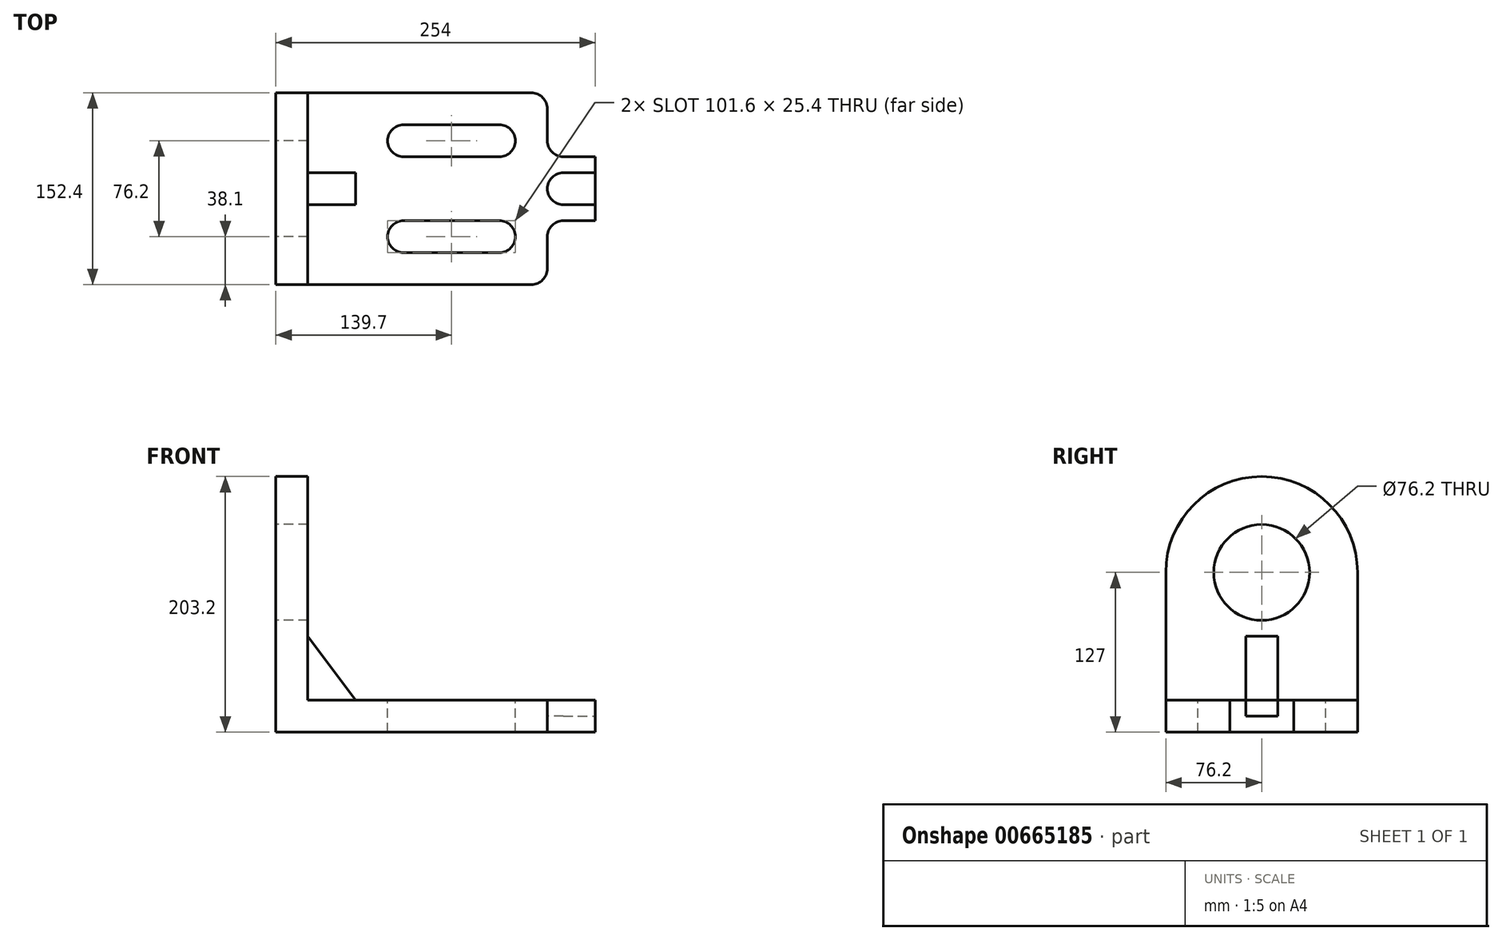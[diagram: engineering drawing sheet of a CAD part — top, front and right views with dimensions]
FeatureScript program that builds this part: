
annotation { "Feature Type Name" : "Feature", "Feature Type Description" : "" }
export const myFeature = defineFeature(function(context is Context, id is Id, definition is map)
    precondition{}
    {
        {
            var Q0;
            Q0=qCreatedBy(makeId("Top.planeOp"),FACE);
            var sketch = newSketch(context, id + "F0", { "sketchPlane" : qUnion([Q0])});
            skLineSegment(sketch, "E0", {"start": v(0, 0) * mm, "end": v(203.2, 0) * mm});
            skLineSegment(sketch, "E1", {"start": v(215.9, 12.7) * mm, "end": v(215.9, 38.1) * mm});
            skLineSegment(sketch, "E2", {"start": v(228.6, 50.8) * mm, "end": v(254, 50.8) * mm});
            skLineSegment(sketch, "E3", {"start": v(254, 50.8) * mm, "end": v(254, 101.6) * mm});
            skLineSegment(sketch, "E4", {"start": v(254, 101.6) * mm, "end": v(228.6, 101.6) * mm});
            skLineSegment(sketch, "E5", {"start": v(215.9, 114.3) * mm, "end": v(215.9, 139.7) * mm});
            skLineSegment(sketch, "E6", {"start": v(203.2, 152.4) * mm, "end": v(0, 152.4) * mm});
            skLineSegment(sketch, "E7", {"start": v(0, 152.4) * mm, "end": v(0, 0) * mm});
            skLineSegment(sketch, "E8", {"start": v(254, 76.2) * mm, "end": v(228.6, 76.2) * mm, "construction": true});
            skArc(sketch, "E9", {"start": v(228.6, 88.9) * mm, "mid": v(215.9, 76.2) * mm, "end": v(228.6, 63.5) * mm});
            skLineSegment(sketch, "E10", {"start": v(228.6, 88.9) * mm, "end": v(254, 88.9) * mm});
            skLineSegment(sketch, "E11", {"start": v(228.6, 63.5) * mm, "end": v(254, 63.5) * mm});
            skPoint(sketch, "E12.visualSharp", {"position": v(215.9, 152.4) * mm});
            skArc(sketch, "E12.filletArc", {"start": v(215.9, 139.7) * mm, "mid": v(212.18, 148.68) * mm, "end": v(203.2, 152.4) * mm});
            skPoint(sketch, "E13.visualSharp", {"position": v(215.9, 101.6) * mm});
            skArc(sketch, "E13.filletArc", {"start": v(215.9, 114.3) * mm, "mid": v(219.62, 105.32) * mm, "end": v(228.6, 101.6) * mm});
            skPoint(sketch, "E14.visualSharp", {"position": v(215.9, 50.8) * mm});
            skArc(sketch, "E14.filletArc", {"start": v(228.6, 50.8) * mm, "mid": v(219.62, 47.08) * mm, "end": v(215.9, 38.1) * mm});
            skPoint(sketch, "E15.visualSharp", {"position": v(215.9, 0) * mm});
            skArc(sketch, "E15.filletArc", {"start": v(203.2, 0) * mm, "mid": v(212.18, 3.72) * mm, "end": v(215.9, 12.7) * mm});
            skLineSegment(sketch, "E16.0", {"start": v(25.4, 38.1) * mm, "end": v(177.8, 38.1) * mm, "construction": true});
            skLineSegment(sketch, "E17.0", {"start": v(101.6, 114.3) * mm, "end": v(101.6, 38.1) * mm, "construction": true});
            skLineSegment(sketch, "E18.0", {"start": v(177.8, 114.3) * mm, "end": v(177.8, 38.1) * mm, "construction": true});
            skArc(sketch, "E19", {"start": v(177.8, 101.6) * mm, "mid": v(190.5, 114.3) * mm, "end": v(177.8, 127) * mm});
            skArc(sketch, "E20", {"start": v(101.6, 127) * mm, "mid": v(88.9, 114.3) * mm, "end": v(101.6, 101.6) * mm});
            skArc(sketch, "E21", {"start": v(177.8, 25.4) * mm, "mid": v(190.5, 38.1) * mm, "end": v(177.8, 50.8) * mm});
            skArc(sketch, "E22", {"start": v(101.6, 50.8) * mm, "mid": v(88.9, 38.1) * mm, "end": v(101.6, 25.4) * mm});
            skLineSegment(sketch, "E23", {"start": v(101.6, 127) * mm, "end": v(177.8, 127) * mm});
            skLineSegment(sketch, "E24", {"start": v(101.6, 101.6) * mm, "end": v(177.8, 101.6) * mm});
            skLineSegment(sketch, "E25", {"start": v(101.6, 50.8) * mm, "end": v(177.8, 50.8) * mm});
            skLineSegment(sketch, "E26", {"start": v(101.6, 25.4) * mm, "end": v(177.8, 25.4) * mm});
            skLineSegment(sketch, "E27.0", {"start": v(177.8, 114.3) * mm, "end": v(0, 114.3) * mm, "construction": true});
            skLineSegment(sketch, "E28.0", {"start": v(25.4, 152.4) * mm, "end": v(25.4, 0) * mm, "construction": true});
            skLineSegment(sketch, "E29.0", {"start": v(63.5, 88.9) * mm, "end": v(25.4, 88.9) * mm});
            skLineSegment(sketch, "E30.0", {"start": v(63.5, 63.5) * mm, "end": v(25.4, 63.5) * mm});
            skLineSegment(sketch, "E31", {"start": v(63.5, 88.9) * mm, "end": v(63.5, 63.5) * mm});
            skLineSegment(sketch, "E32", {"start": v(25.4, 88.9) * mm, "end": v(25.4, 63.5) * mm});
            skSolve(sketch);
        }
        {
            var Q0;
            Q0=makeQuery(id+"F0.imprint","IMPRINT",FACE,{"disambiguationData":[TD([[makeQuery(id+"F0.imprint","IMPRINT",EDGE,{"derivedFrom":sQuery(id+"F0.wireOp",EDGE,"E0")}),1.0]])]});
            var Q1;
            Q1=makeQuery(id+"F0.imprint","IMPRINT",FACE,{"disambiguationData":[TD([[makeQuery(id+"F0.imprint","IMPRINT",EDGE,{"derivedFrom":sQuery(id+"F0.wireOp",EDGE,"E9")}),1.0]])]});
            var Q2;
            Q2=makeQuery(id+"F0.imprint","IMPRINT",FACE,{"disambiguationData":[TD([[makeQuery(id+"F0.imprint","IMPRINT",EDGE,{"derivedFrom":sQuery(id+"F0.wireOp",EDGE,"E29.0")}),1.0]])]});
            extrude(context, id + "F1", {"entities" : qUnion([Q0, Q1, Q2]), "oppositeDirection" : true, "depth" : 25.4 * mm, "offsetDistance" : 25.4 * mm});
        }
        {
            var Q0;
            Q0=makeQuery(id+"F1.opExtrude","SWEPT_FACE",FACE,{"disambiguationData":[OSD([sQuery(id+"F0.wireOp",EDGE,"E7")])]});
            var sketch = newSketch(context, id + "F2", { "sketchPlane" : qUnion([Q0])});
            skPoint(sketch, "E33.centerSnap0", {"position": v(-76.2, 0) * mm});
            skLineSegment(sketch, "E34", {"start": v(-152.4, 0) * mm, "end": v(-152.4, 101.6) * mm});
            skLineSegment(sketch, "E35", {"start": v(0, 0) * mm, "end": v(0, 101.6) * mm});
            skArc(sketch, "E36", {"start": v(0, 101.6) * mm, "mid": v(-76.2, 177.8) * mm, "end": v(-152.4, 101.6) * mm});
            skCircle(sketch, "E37", {"center": v(-76.2, 101.6) * mm, "radius": 38.1 * mm});
            skSolve(sketch);
        }
        {
            var Q0;
            Q0=makeQuery(id+"F2.imprint","IMPRINT",FACE,{"disambiguationData":[TD([[makeQuery(id+"F2.imprint","IMPRINT",EDGE,{"derivedFrom":sQuery(id+"F2.wireOp",EDGE,"E34")}),-1.0]])]});
            extrude(context, id + "F3", {"entities" : qUnion([Q0]), "operationType" : NewBodyOperationType.ADD, "oppositeDirection" : true, "depth" : 25.4 * mm, "offsetDistance" : 25.4 * mm});
        }
        {
            var Q0;
            Q0=makeQuery(id+"F0.imprint","IMPRINT",FACE,{"disambiguationData":[TD([[makeQuery(id+"F0.imprint","IMPRINT",EDGE,{"derivedFrom":sQuery(id+"F0.wireOp",EDGE,"E9")}),1.0]])]});
            extrude(context, id + "F4", {"entities" : qUnion([Q0]), "operationType" : NewBodyOperationType.REMOVE, "oppositeDirection" : true, "depth" : 12.7 * mm, "offsetDistance" : 25.4 * mm});
        }
        {
            var Q0;
            Q0=makeQuery(id+"F0.imprint","IMPRINT",FACE,{"disambiguationData":[TD([[makeQuery(id+"F0.imprint","IMPRINT",EDGE,{"derivedFrom":sQuery(id+"F0.wireOp",EDGE,"E29.0")}),1.0]])]});
            extrude(context, id + "F5", {"entities" : qUnion([Q0]), "operationType" : NewBodyOperationType.ADD, "depth" : 50.8 * mm, "offsetDistance" : 25.4 * mm});
        }
        {
            var Q0;
            Q0=makeQuery(id+"F5.opExtrude","SWEPT_FACE",FACE,{"disambiguationData":[OSD([sQuery(id+"F0.wireOp",EDGE,"E30.0")])]});
            var sketch = newSketch(context, id + "F6", { "sketchPlane" : qUnion([Q0])});
            skLineSegment(sketch, "E38", {"start": v(63.5, 0) * mm, "end": v(25.4, 50.8) * mm});
            skLineSegment(sketch, "E39", {"start": v(25.4, 50.8) * mm, "end": v(63.5, 50.8) * mm});
            skLineSegment(sketch, "E40", {"start": v(63.5, 50.8) * mm, "end": v(63.5, 0) * mm});
            skSolve(sketch);
        }
        {
            var Q0;
            Q0=makeQuery(id+"F6.imprint","IMPRINT",FACE,{"disambiguationData":[TD([[makeQuery(id+"F6.imprint","IMPRINT",EDGE,{"derivedFrom":sQuery(id+"F6.wireOp",EDGE,"E38")}),-1.0]])]});
            extrude(context, id + "F7", {"entities" : qUnion([Q0]), "operationType" : NewBodyOperationType.REMOVE, "oppositeDirection" : true, "depth" : 25.4 * mm, "offsetDistance" : 25.4 * mm});
        }
    });
